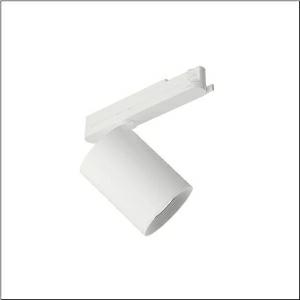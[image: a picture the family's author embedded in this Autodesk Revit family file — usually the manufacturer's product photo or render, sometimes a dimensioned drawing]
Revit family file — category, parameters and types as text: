
# Revit family: spot_21_51se13mbb5b
name_source: partatom
category: Lighting Fixtures
units: mm (PartAtom-declared; Revit-internal decimal feet)

## family parameters
Cut with Voids When Loaded = No
Host = Face
Light Source = No
Part Type = Normal
Room Calculation Point = No
Round Connector Dimension = Use Diameter
Shared = No

## types (1)
- --- (1 x LED, 5350 lm, 41.8 W, 3000K)
    Apparent Load = 42 VA
    CIE Flux Codes = 95 98 99 100 100
    Color Rendering = 90
    Color Temperature = 3000K
    Default Elevation = 1800 mm
    Description = Spot 21, directional spotlight, light control with lens, of PMMA, LED rated luminous flux: 5.140lm, light colour: 930, control gear: ECG Multilumen, with 3-phase adapter, mains connection: 220..240V, AC, 50/60Hz, of aluminium, traffic white (RAL 9016), length: 213mm, diameter: 105mm, protection rating (complete): IP20, insulation class (complete): insulation class I (protective earthing), certification: CE, impact resistance: IK02, permissible ambient temperature for indoor applications: -20..+40°C, packaging unit: 1 piece
    Height = 175 mm
    Lamp = 1 x LED
    Lamp Light Flux = 5350 lm
    Lamp Power = 41.8 W
    Lamp count = 1
    Length = 105 mm
    Luminous efficacy = 128 lm/W
    Manufacturer = Siteco
    ModVariant = No
    Model = 51SE13MBB5B
    Mounting Place = Ceiling
    Mounting Type = Pendant
    Number of Poles = 1
    OnlyDefault = Yes
    Power Factor = 1
    Product Name = Spot 21
    Product group = directional spotlight
    ProductGroupID = 905
    Protection Class = Protection class I
    Protection Degree = IP 20
    RLX_Detail_Level = 1
    RLX_Emergency_Light_Flux = 0 lm
    RLX_Emergency_Type = 0
    RLX_Emergency_Type_DB = No
    RlxData = <blob elided: 17657 chars, md5=4b4f5cdf>
    Socket = socket
    Standby Power = 0 W
    System Light Flux = 5350 lm
    System Power = 42 W
    Type Comments = factory setting: luminous flux: 100 % | (ON | ON | ON | ON) | 1050 mA
    Type Image = l_1003976.jpg
    URL = http://relux.com
    VarID = @adj_165665
    Voltage = 0 V
    Weight = 0.00 kg
    Width = 0 mm  [stored 0 ft]

note: [stored X ft] marks values corroborated as IEEE doubles in the binary element streams (Revit-internal decimal feet)

## geometry (parser evidence)
native form markers: Blend x4, Sweep x10
no freeform markers — native parametric forms only
